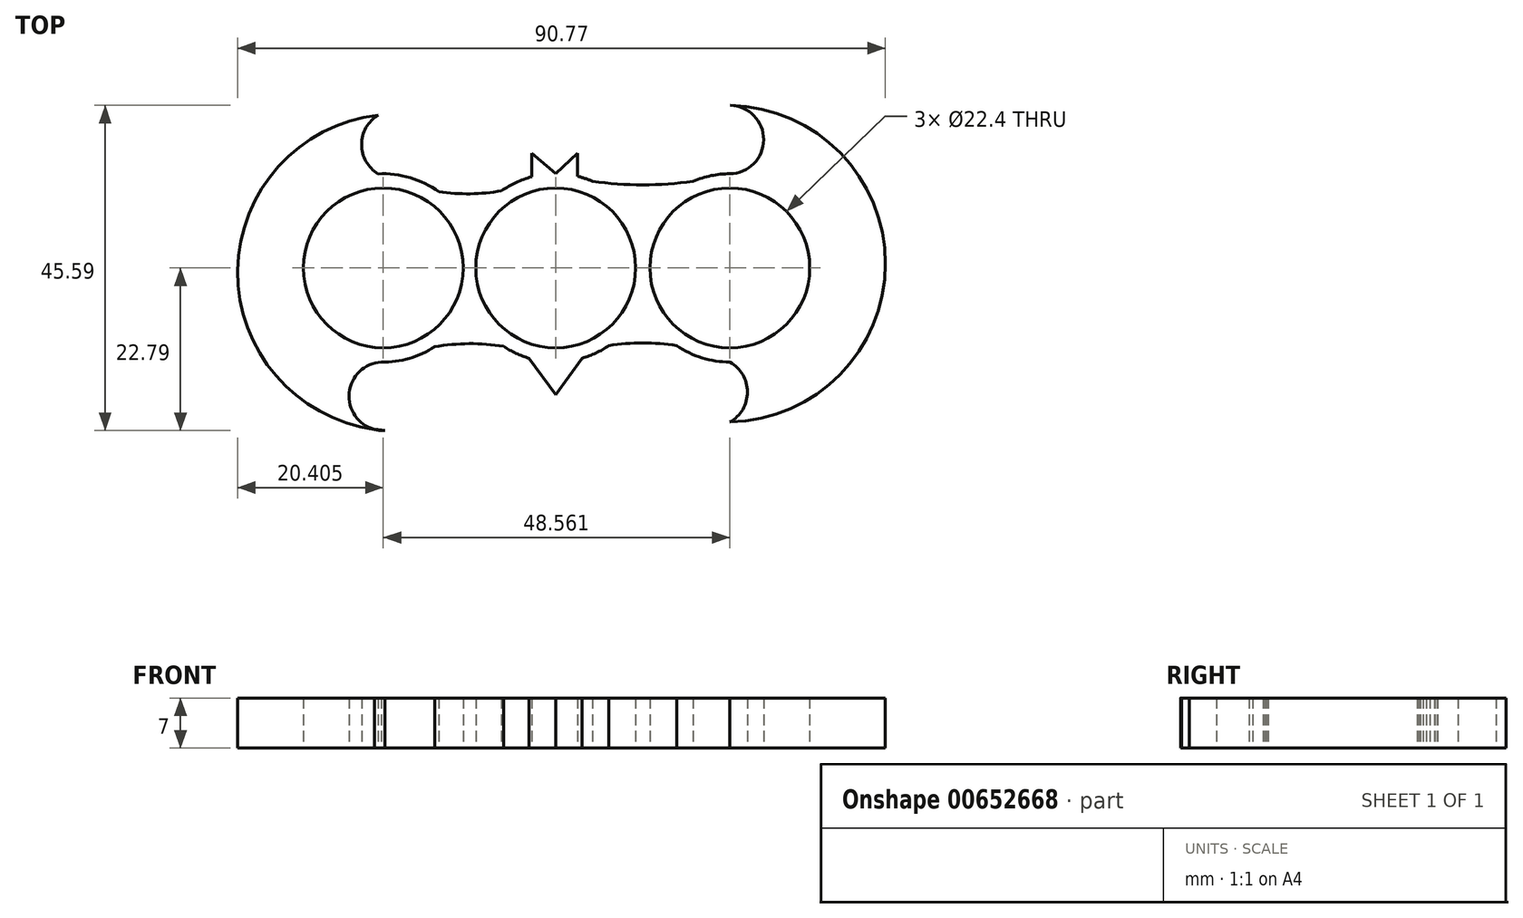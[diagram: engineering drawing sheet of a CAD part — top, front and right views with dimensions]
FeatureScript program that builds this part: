
annotation { "Feature Type Name" : "Feature", "Feature Type Description" : "" }
export const myFeature = defineFeature(function(context is Context, id is Id, definition is map)
    precondition{}
    {
        {
            var Q0;
            Q0=qCreatedBy(makeId("Top.planeOp"),FACE);
            var sketch = newSketch(context, id + "F0", { "sketchPlane" : qUnion([Q0])});
            skCircle(sketch, "E0", {"center": v(0, 0) * mm, "radius": 11.2 * mm});
            skCircle(sketch, "E1", {"center": v(24.4, 0) * mm, "radius": 11.2 * mm});
            skCircle(sketch, "E2", {"center": v(24.4, 0) * mm, "radius": 13.2 * mm});
            skCircle(sketch, "E3", {"center": v(0, 0) * mm, "radius": 13.2 * mm});
            skCircle(sketch, "E4", {"center": v(-24.16, 0) * mm, "radius": 11.2 * mm});
            skCircle(sketch, "E5", {"center": v(-24.16, 0) * mm, "radius": 13.2 * mm});
            skArc(sketch, "E6", {"start": v(-24.86, 13.18) * mm, "mid": v(-12.43, 10.4) * mm, "end": v(0, 13.2) * mm});
            skArc(sketch, "E7", {"start": v(0, -13.2) * mm, "mid": v(-11.95, -10.62) * mm, "end": v(-23.9, -13.2) * mm});
            skArc(sketch, "E8", {"start": v(24.4, -13.2) * mm, "mid": v(12.2, -10.5) * mm, "end": v(0, -13.2) * mm});
            skArc(sketch, "E9", {"start": v(0, 13.2) * mm, "mid": v(12.2, 11.64) * mm, "end": v(24.4, 13.2) * mm});
            skArc(sketch, "E10", {"start": v(24.4, 13.2) * mm, "mid": v(29.13, 18) * mm, "end": v(24.4, 22.8) * mm});
            skArc(sketch, "E11", {"start": v(24.4, -21.6) * mm, "mid": v(26.87, -17.4) * mm, "end": v(24.4, -13.2) * mm});
            skArc(sketch, "E12", {"start": v(24.4, -21.6) * mm, "mid": v(46.2, 0.6) * mm, "end": v(24.4, 22.8) * mm});
            skArc(sketch, "E13", {"start": v(-24.86, 21.42) * mm, "mid": v(-27.2, 17.3) * mm, "end": v(-24.86, 13.18) * mm});
            skArc(sketch, "E14", {"start": v(-23.9, -13.2) * mm, "mid": v(-28.97, -18) * mm, "end": v(-23.9, -22.78) * mm});
            skArc(sketch, "E15", {"start": v(-24.86, 21.42) * mm, "mid": v(-44.56, -1.12) * mm, "end": v(-23.9, -22.78) * mm});
            skLineSegment(sketch, "E16", {"start": v(3.02, 12.85) * mm, "end": v(3.02, 16.07) * mm});
            skLineSegment(sketch, "E17", {"start": v(-3.37, 11.85) * mm, "end": v(-3.37, 16.07) * mm});
            skLineSegment(sketch, "E18", {"start": v(-3.37, 16.07) * mm, "end": v(0, 13.2) * mm});
            skLineSegment(sketch, "E19", {"start": v(3.02, 16.07) * mm, "end": v(0, 13.2) * mm});
            skLineSegment(sketch, "E20", {"start": v(-3.71, -12.67) * mm, "end": v(0, -17.76) * mm});
            skLineSegment(sketch, "E21", {"start": v(0, -17.76) * mm, "end": v(3.71, -12.67) * mm});
            skSolve(sketch);
        }
        {
            var Q0;
            Q0 = qSketchRegion(id + "F0", true);
            var Q1;
            {var subQ4=sQuery(id+"F0.wireOp",EDGE,"E5");var subQ6=sQuery(id+"F0.wireOp",EDGE,"E0");var subQ7=makeQuery(id+"F0.imprint","INTERSECT",VERTEX,{"disambiguationData":[OD(0.0)],"derivedFrom":[subQ6,subQ4]});Q1=makeQuery(id+"F0.imprint","IMPRINT",FACE,{"disambiguationData":[TD([[makeQuery(id+"F0.imprint","IMPRINT",EDGE,{"disambiguationData":[TD([[subQ7,-1.0]])],"derivedFrom":subQ6}),-1.0]])]});}
            var Q2;
            {var subQ0=sQuery(id+"F0.wireOp",EDGE,"E2");var subQ1=sQuery(id+"F0.wireOp",EDGE,"E0");var subQ8=makeQuery(id+"F0.imprint","INTERSECT",VERTEX,{"disambiguationData":[OD(0.0)],"derivedFrom":[subQ1,subQ0]});Q2=makeQuery(id+"F0.imprint","IMPRINT",FACE,{"disambiguationData":[TD([[makeQuery(id+"F0.imprint","IMPRINT",EDGE,{"disambiguationData":[TD([[subQ8,1.0]])],"derivedFrom":subQ1}),-1.0]])]});}
            extrude(context, id + "F1", {"entities" : qUnion([Q0, Q1, Q2]), "depth" : 7 * mm, "offsetDistance" : 25 * mm});
        }
    });
